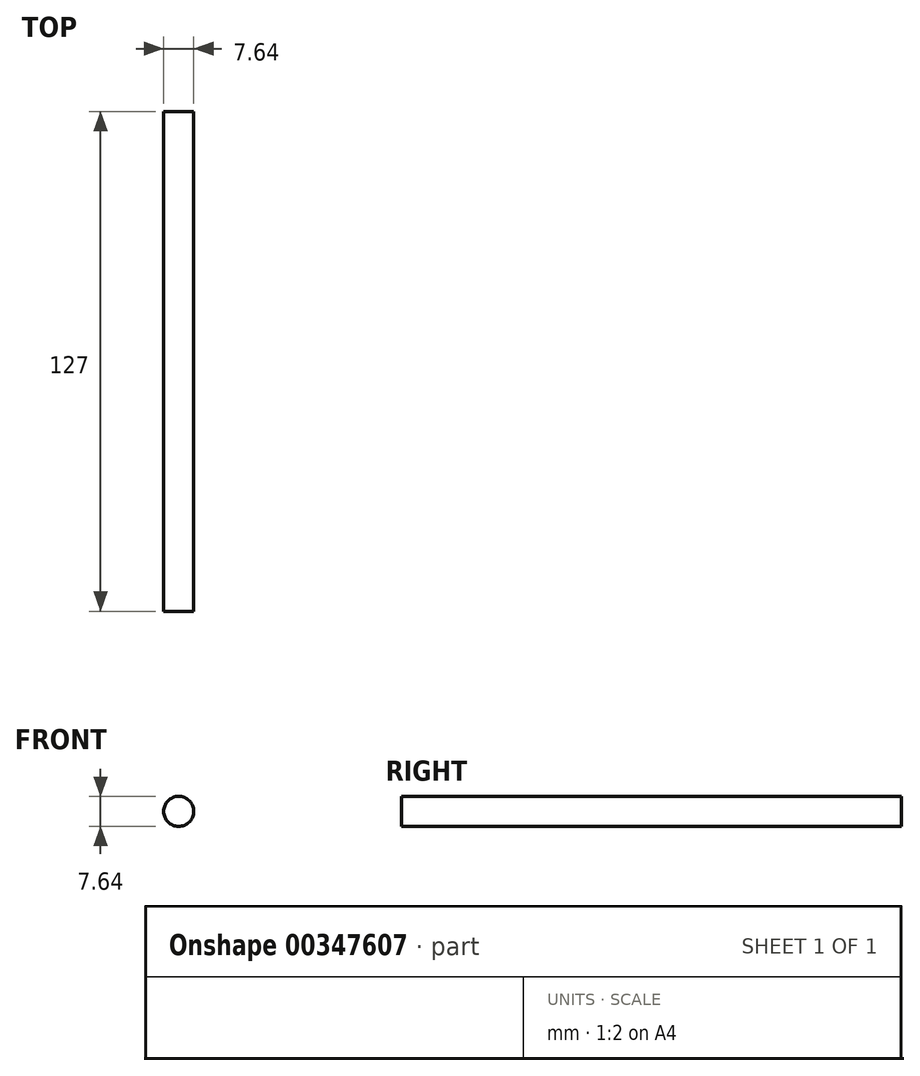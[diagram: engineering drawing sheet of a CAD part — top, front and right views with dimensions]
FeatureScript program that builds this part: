
annotation { "Feature Type Name" : "Feature", "Feature Type Description" : "" }
export const myFeature = defineFeature(function(context is Context, id is Id, definition is map)
    precondition{}
    {
        {
            var Q0;
            Q0=qCreatedBy(makeId("Front.planeOp"),FACE);
            var sketch = newSketch(context, id + "F0", { "sketchPlane" : qUnion([Q0])});
            skCircle(sketch, "E0", {"center": v(0, 0) * mm, "radius": 3.82 * mm});
            skSolve(sketch);
        }
        {
            var Q0;
            Q0=makeQuery(id+"F0.imprint","IMPRINT",FACE,{"disambiguationData":[TD([[makeQuery(id+"F0.imprint","IMPRINT",EDGE,{"derivedFrom":sQuery(id+"F0.wireOp",EDGE,"E0")}),1.0]])]});
            extrude(context, id + "F1", {"entities" : qUnion([Q0]), "depth" : 127 * mm});
        }
    });
